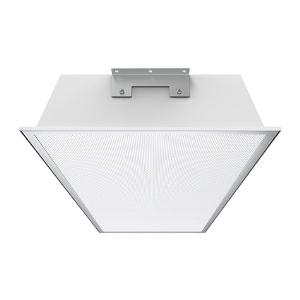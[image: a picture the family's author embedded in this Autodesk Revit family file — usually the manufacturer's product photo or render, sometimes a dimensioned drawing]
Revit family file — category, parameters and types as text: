
# Revit family: 3f_filippi_-_beta_500_sp_3f_filippi_-_52003_-_beta_500_300w-840_sp_l1230
name_source: partatom
category: Lighting Fixtures
units: mm (PartAtom-declared; Revit-internal decimal feet)

## family parameters
Cut with Voids When Loaded = No
Host = Face
Light Source = No
Part Type = Normal
Room Calculation Point = No
Round Connector Dimension = Use Diameter
Shared = No

## types (1)
- 3F Filippi - Beta 500 SP (1 x LED, 45194 lm, 298 W, 4000 K)
    Apparent Load = 298 VA
    Approval mark = CE
    CIE Flux Codes = 64 89 97 100 100
    Color Rendering = 80
    Color Temperature = 4000 K
    Control Gear = Electronic ballast
    Default Elevation = 1800 mm
    Description = ILLUMINOTECHNICAL
Luminous efficiency 100% (DLOR 100%, ULOR 0%).
Initial luminous flux of the luminaire 45194 lm.
Direct symmetric medium distribution.
Installation Interdistance Transv.D = 1.19 x hu - Long.D = 1.23 x hu.
Tabular UGR (CIE 117 - 4H-8H; S=0.25H; 70/50/20): RUG 24.4 - 24.7.
Beam angle: 82° - 90°.
Luminous efficacy 152 lm/W.
Lifetime (L93/B10): 30000 h. (tq+25°C)
Lifetime (L90/B10): 50000 h. (tq+25°C)
Lifetime (L85/B10): 80000 h. (tq+25°C)
Lifetime (L80/B10): 100000 h. (tq+25°C)
Lifetime (L85/B10): 50000 h. (tq+45°C)
Sudden decreased luminous flux after 50000 hours: 0% (C0).
Photobiological safety in compliance with IEC/TR 62778: RG0 risk exempt, (IEC 62471).
In compliance with IEC/EN 62722-2-1 - IEC/EN 62717 standards.

SOURCE
3 linear LED modules 100W/840.
Energy efficiency class (UE 2019/2020 - UE 2019/2015): C.
CIE 13.3 Colour rendering index: CRI >80 (R9 <50%).
IES TM-30 Fidelity Index: Rf = 84 Rg = 95.
CCT nominal colour temperature 4000 K.
Colour initial tolerance (MacAdam): SDCM 3.

MECHANICAL
Housing in white painted epoxy-polyester powder aluminium.
White aluminium non-iridescent high efficiency.
SP transparent methacrylate (PMMA) diffuser, prismatic outside, antiglare.
Perimetrical frame in stainless steel with vandal-proof opening and stainless steel nuts and bolts.
Polyurethane foam seal, ecological, anti-aging, installed using a continuous automatic process with no joints.
Fixing bracket in stainless steel.
Luminaire with limited surface temperature. - D - (EN 60598-2-24)
Dimensions: 1230x475 mm, height 130 mm. Weight 12.425 kg.
IP66 protection degree.
Mechanical strength to impacts IK07 (2 joule).
Glow-wire test resistance 850°C.

ELECTRICAL
Halogen Free electronic wiring 230V-50/60Hz, power factor 0.95, THD <25%, constant output current, class I, 3 driver.
Twin-circuit.
Power of the luminaire 298 W.
ENEC - CE.
SAFE FLICKER: PstLM=<1 and SVM=<0.4 (IEC TR 61547-1 and IEC TR 63158), to ensure a more comfortable and safe light.
Luminaire compliant with EN 60598-2-22 for power supply from a centralised emergency system CPSS (Central Power Supply System), not incorporated in the luminaire - high risk areas excluded. The default power and flux are 100% in AC and 100% in DC.
Ambient temperature from -20°C to +45°C.
Temperature class T6 max 85°C.
Quick connection via M20 3P connector with 9-13 mm tightening range.
Quick connection in polycarbonate with M20x1,5 cable gland, to access the terminal block positioned on a removable runner.
Relative humidity UR: <85%.

INSTALLATION
Ceiling / Suspended.
All accessories dedicated to this product are available on the Catalog and on our website www.3F-Filippi.com.

APPLICATIONS
Suitable product for food production plants (HACCP), IFS (Food Version 6), BRC (GSFS Food Version 7).
Commercial and industrial environments and warehouses.

WARNING
Fixture not suitable for cold stores with an ambient temperature <0°C and/or relative humidity >85%.
Luminaire designed for disposal/recycling at end-of-life.
Replaceable (LED only) light source by a professional. Replaceable control gear by a professional.
    Height = 130 mm
    Lamp = 1 x LED
    Lamp Light Flux = 45194 lm
    Lamp Power = 298 W
    Lamp count = 1
    Length = 1230 mm
    Lifetime = 50000 h
    Luminous efficacy = 152 lm/W
    Manufacturer = 3F Filippi
    ModVariant = No
    Model = 3F Filippi - 52003 - Beta 500 300W-840 SP L1230
    Mounting Place = Ceiling
    Mounting Type = Pendant
    Number of Poles = 1
    OnlyDefault = Yes
    Power Factor = 1
    Product Name = 3F Filippi - Beta 500 SP
    Product group = pendant luminaire
    ProductGroupID = 9
    Protection Class = Protection class I
    Protection Degree = IP 66
    RLX_Detail_Level = 1
    RLX_Emergency_Light_Flux = 0 lm
    RLX_Emergency_Type = 0
    RLX_Emergency_Type_DB = No
    RlxData = <blob elided: 132889 chars, md5=e81d6cdd>
    Socket = socket
    Standby Power = 0 W
    System Light Flux = 45195 lm
    System Power = 298 W
    Type Comments = Product without accessories
    Type Image = 3ffilippi_beta_500_sp_pc.jpg
    URL = http://relux.com
    VarID = ---
    Voltage = 0 V
    Weight = 0.00 kg
    Width = 475 mm

## geometry (parser evidence)
native form markers: Blend x4, Sweep x10
no freeform markers — native parametric forms only
